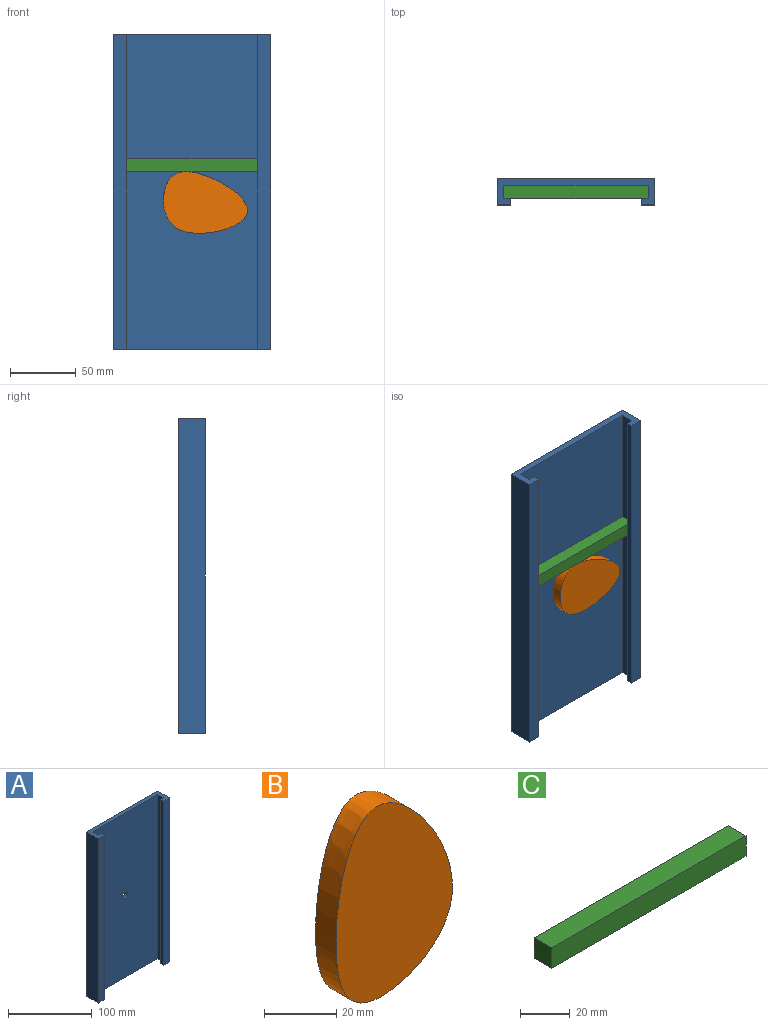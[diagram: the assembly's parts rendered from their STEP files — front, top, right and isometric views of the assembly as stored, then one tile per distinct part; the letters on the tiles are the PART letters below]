
ASSEMBLY  parts=3 mates=2
PART A: 15 faces, bbox 120x20x240 mm
  f0: plane 240x5mm, normal (1,0,0), area 1200mm2, adj f1,f3,f8,f13
  f1: plane 120x20mm, normal (0,0,-1), area 800mm2, adj f0,f2,f4,f5,f6,f7,f8,f9
  f2: plane 240x5mm, normal (-1,0,0), area 1200mm2, adj f1,f3,f6,f11
  f3: plane 120x20mm, normal (0,0,1), area 800mm2, adj f0,f2,f4,f5,f6,f7,f8,f9
  f4: plane 240x110mm, normal (0,-1,0), area 26321.5mm2, adj f1,f3,f5,f7,f14
  f5: plane 240x10mm, normal (-1,0,0), area 2400mm2, adj f1,f3,f4,f6
  f6: plane 240x5mm, normal (0,1,0), area 1200mm2, adj f1,f2,f3,f5
  f7: plane 240x10mm, normal (1,0,0), area 2400mm2, adj f1,f3,f4,f8
  f8: plane 240x5mm, normal (0,1,0), area 1200mm2, adj f0,f1,f3,f7
  f9: plane 240x120mm, normal (0,1,0), area 28721.5mm2, adj f1,f3,f10,f12,f14
  f10: plane 240x20mm, normal (1,0,0), area 4800mm2, adj f1,f3,f9,f11
  f11: plane 240x10mm, normal (0,-1,0), area 2400mm2, adj f1,f2,f3,f10
  f12: plane 240x20mm, normal (-1,0,0), area 4800mm2, adj f1,f3,f9,f13
  f13: plane 240x10mm, normal (0,-1,0), area 2400mm2, adj f0,f1,f3,f12
  f14: cylinder r=5mm len=10mm, axis (0,-1,0), area 157.1mm2, adj f4,f9
PART B: 5 faces, bbox 51x15x69 mm
  f0: plane 10x10mm, normal (0,1,0), area 78.5mm2, adj f1
  f1: cylinder r=5mm len=10mm, axis (0,-1,0), area 219.9mm2, adj f0,f4
  f2: extruded ~65.1x45.46mm, area 1405.8mm2, adj f3,f4
  f3: plane 69.02x51.05mm, normal (0,-1,0), area 2271.9mm2, adj f2
  f4: plane 69.02x51.05mm, normal (0,1,0), area 2193.4mm2, adj f1,f2
PART C: 6 faces, bbox 110x10x10 mm
  f0: plane 10x10mm, normal (1,0,0), area 100mm2, adj f1,f2,f4,f5
  f1: plane 110x10mm, normal (0,0,1), area 1100mm2, adj f0,f3,f4,f5
  f2: plane 110x10mm, normal (0,0,-1), area 1100mm2, adj f0,f3,f4,f5
  f3: plane 10x10mm, normal (-1,0,0), area 100mm2, adj f1,f2,f4,f5
  f4: plane 110x10mm, normal (0,1,0), area 1100mm2, adj f0,f1,f2,f3
  f5: plane 110x10mm, normal (0,-1,0), area 1100mm2, adj f0,f1,f2,f3
PLACE A at identity fixed
PLACE B rot(axis=(0,1,0),111.1deg) t=(-43.27,0,-111.93)mm
PLACE C rot(axis=(-0.01,-0.99,0.11),0deg) t=(0,0,-94.51)mm
MATE revolute A.f14 <-> B.f1  axis (0,1,0) through (0,7,0)mm
MATE slider A.f3 <-> C.f1  axis (0,0,1) through (-55,2,120)mm
